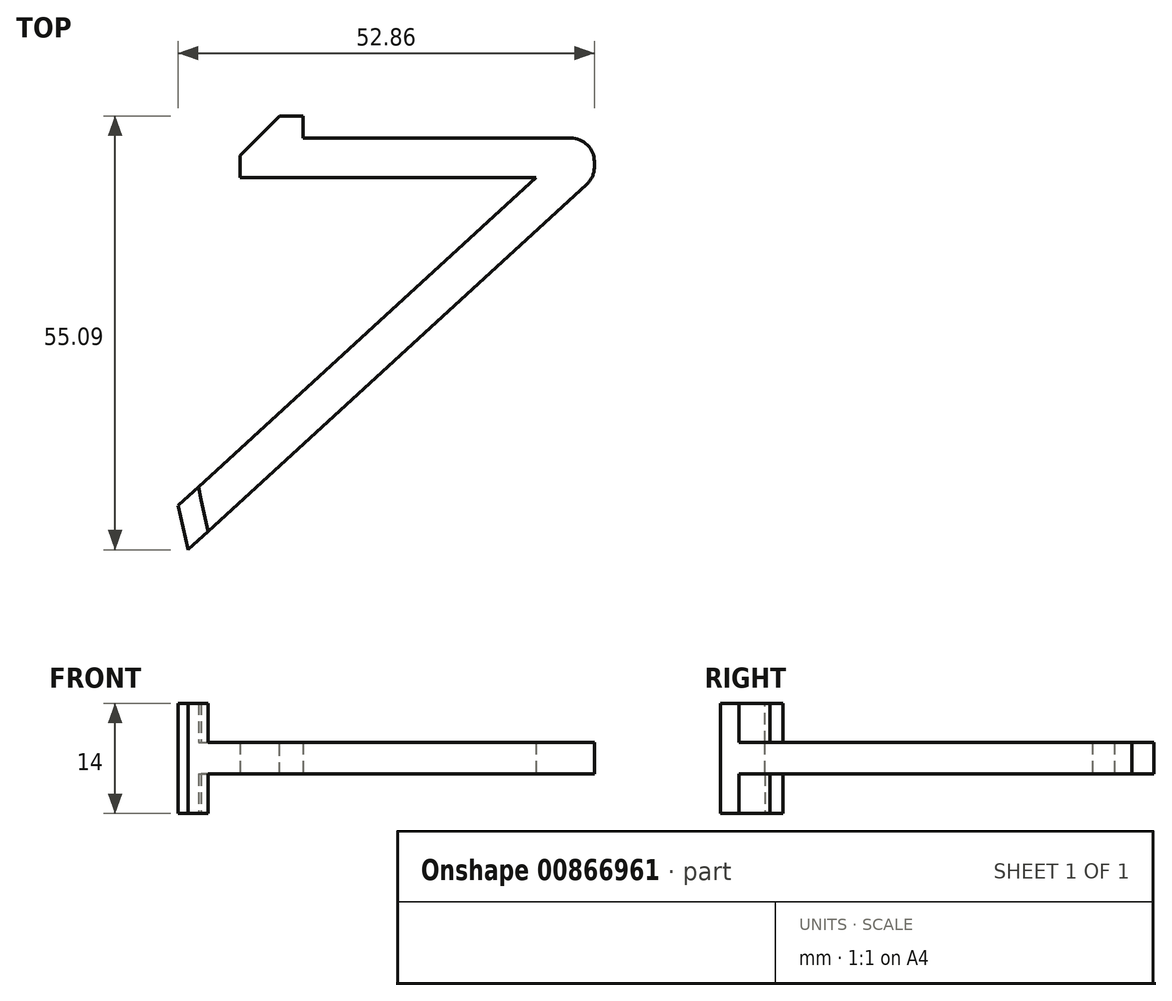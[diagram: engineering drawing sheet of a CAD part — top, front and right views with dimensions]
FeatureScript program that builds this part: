
annotation { "Feature Type Name" : "Feature", "Feature Type Description" : "" }
export const myFeature = defineFeature(function(context is Context, id is Id, definition is map)
    precondition{}
    {
        {
            var Q0;
            Q0=qCreatedBy(makeId("Top.planeOp"),FACE);
            var sketch = newSketch(context, id + "F0", { "sketchPlane" : qUnion([Q0])});
            skLineSegment(sketch, "E0", {"start": v(-40, 0) * mm, "end": v(0, 0) * mm});
            skLineSegment(sketch, "E1", {"start": v(0, 0) * mm, "end": v(0, -5) * mm});
            skLineSegment(sketch, "E2", {"start": v(0, -5) * mm, "end": v(-40, -5) * mm});
            skLineSegment(sketch, "E3", {"start": v(-40, -5) * mm, "end": v(-40, 0) * mm});
            skLineSegment(sketch, "E4", {"start": v(0, -5) * mm, "end": v(-51.6, -52.3) * mm});
            skLineSegment(sketch, "E5", {"start": v(-40, 0) * mm, "end": v(-45, 0) * mm});
            skLineSegment(sketch, "E6", {"start": v(-45, 0) * mm, "end": v(-45, -5) * mm});
            skLineSegment(sketch, "E7", {"start": v(-45, -5) * mm, "end": v(-40, -5) * mm});
            skLineSegment(sketch, "E8", {"start": v(-51.6, -52.3) * mm, "end": v(-54.99, -48.6) * mm});
            skLineSegment(sketch, "E9", {"start": v(-54.99, -48.6) * mm, "end": v(-7.4, -5) * mm});
            skLineSegment(sketch, "E10", {"start": v(-51.6, -52.3) * mm, "end": v(-52.86, -46.65) * mm});
            skSolve(sketch);
        }
        {
            var Q0;
            Q0=makeQuery(id+"F0.imprint","IMPRINT",FACE,{"disambiguationData":[TD([[makeQuery(id+"F0.imprint","IMPRINT",EDGE,{"derivedFrom":sQuery(id+"F0.wireOp",EDGE,"E0")}),-1.0]])]});
            var Q1;
            {var subQ0=sQuery(id+"F0.wireOp",EDGE,"E4");Q1=makeQuery(id+"F0.imprint","IMPRINT",FACE,{"disambiguationData":[TD([[makeQuery(id+"F0.imprint","IMPRINT",EDGE,{"derivedFrom":subQ0}),-1.0]])]});}
            var Q2;
            Q2=makeQuery(id+"F0.imprint","IMPRINT",FACE,{"disambiguationData":[TD([[makeQuery(id+"F0.imprint","IMPRINT",EDGE,{"derivedFrom":sQuery(id+"F0.wireOp",EDGE,"E3")}),1.0]])]});
            extrude(context, id + "F1", {"entities" : qUnion([Q0, Q1, Q2]), "depth" : 4 * mm, "offsetDistance" : 25 * mm});
        }
        {
            var Q0;
            Q0=makeQuery(id+"F1.opExtrude","SWEPT_EDGE",EDGE,{"disambiguationData":[OSD([sQuery(id+"F0.wireOp",EDGE,"E0"),sQuery(id+"F0.wireOp",EDGE,"E1")])]});
            var Q1;
            Q1=makeQuery(id+"F1.opExtrude","SWEPT_EDGE",EDGE,{"disambiguationData":[OSD([sQuery(id+"F0.wireOp",EDGE,"E1"),sQuery(id+"F0.wireOp",EDGE,"E2"),sQuery(id+"F0.wireOp",EDGE,"E4")])]});
            fillet(context, id + "F2", {"entities" : qUnion([Q0, Q1]), "radius" : 3 * mm, "tangentPropagation" : true, "allowEdgeOverflow" : false});
        }
        {
            var Q0;
            Q0=qCreatedBy(makeId("Front.planeOp"),FACE);
            var sketch = newSketch(context, id + "F3", { "sketchPlane" : qUnion([Q0])});
            skLineSegment(sketch, "E11", {"start": v(-45, 0) * mm, "end": v(0, 0) * mm});
            skLineSegment(sketch, "E12", {"start": v(-45, 0) * mm, "end": v(-45, 4) * mm});
            skLineSegment(sketch, "E13", {"start": v(-45, 4) * mm, "end": v(-37, 4) * mm});
            skLineSegment(sketch, "E14", {"start": v(-37, 4) * mm, "end": v(-37, 0) * mm});
            skSolve(sketch);
        }
        {
            var Q0;
            {var subQ0=sQuery(id+"F3.wireOp",EDGE,"E12");Q0=makeQuery(id+"F3.imprint","IMPRINT",FACE,{"disambiguationData":[TD([[makeQuery(id+"F3.imprint","IMPRINT",EDGE,{"derivedFrom":subQ0}),-1.0]])]});}
            extrude(context, id + "F4", {"entities" : qUnion([Q0]), "operationType" : NewBodyOperationType.ADD, "oppositeDirection" : true, "depth" : (6.8 - 4) * mm, "offsetDistance" : 25 * mm});
        }
        {
            var Q0;
            Q0=makeQuery(id+"F4.opExtrude","CAP_EDGE",EDGE,{"disambiguationData":[OSD([sQuery(id+"F3.wireOp",EDGE,"E12")])],"isStart":false});
            chamfer(context, id + "F5", {"entities" : qUnion([Q0]), "width" : 5 * mm, "tangentPropagation" : true});
        }
        {
            var Q0;
            Q0=makeQuery(id+"F1.opExtrude","SWEPT_FACE",FACE,{"disambiguationData":[OSD([sQuery(id+"F0.wireOp",EDGE,"E10")])]});
            cPlane(context, id + "F6", {"entities" : qUnion([Q0]), "cplaneType" : CPlaneType.OFFSET, "offset" : 0 * mm, "width" : 150 * mm, "height" : 150 * mm});
        }
        {
            var Q0;
            Q0=qCreatedBy(id+"F6.planeOp",FACE);
            var sketch = newSketch(context, id + "F7", { "sketchPlane" : qUnion([Q0])});
            skLineSegment(sketch, "E15", {"start": v(34.1, 0) * mm, "end": v(34.1, 4) * mm});
            skLineSegment(sketch, "E16", {"start": v(34.1, 4) * mm, "end": v(39.86, 4) * mm});
            skLineSegment(sketch, "E17", {"start": v(39.86, 4) * mm, "end": v(39.86, 0) * mm});
            skLineSegment(sketch, "E18", {"start": v(39.86, 0) * mm, "end": v(34.1, 0) * mm});
            skLineSegment(sketch, "E19", {"start": v(34.1, 0) * mm, "end": v(34.1, -5) * mm});
            skLineSegment(sketch, "E20", {"start": v(34.1, -5) * mm, "end": v(39.86, -5) * mm});
            skLineSegment(sketch, "E21", {"start": v(39.86, -5) * mm, "end": v(39.86, 0) * mm});
            skLineSegment(sketch, "E22", {"start": v(34.1, 4) * mm, "end": v(34.1, 9) * mm});
            skLineSegment(sketch, "E23", {"start": v(34.1, 9) * mm, "end": v(39.86, 9) * mm});
            skLineSegment(sketch, "E24", {"start": v(39.86, 9) * mm, "end": v(39.86, 4) * mm});
            skSolve(sketch);
        }
        {
            var Q0;
            Q0=makeQuery(id+"F7.imprint","IMPRINT",FACE,{"disambiguationData":[TD([[makeQuery(id+"F7.imprint","IMPRINT",EDGE,{"derivedFrom":sQuery(id+"F7.wireOp",EDGE,"E16")}),1.0]])]});
            var Q1;
            Q1=makeQuery(id+"F7.imprint","IMPRINT",FACE,{"disambiguationData":[TD([[makeQuery(id+"F7.imprint","IMPRINT",EDGE,{"derivedFrom":sQuery(id+"F7.wireOp",EDGE,"E18")}),1.0]])]});
            extrude(context, id + "F8", {"entities" : qUnion([Q0, Q1]), "operationType" : NewBodyOperationType.ADD, "oppositeDirection" : true, "depth" : 3 * mm, "offsetDistance" : 25 * mm});
        }
        {
            var Q0;
            Q0=qCreatedBy(makeId("Top.planeOp"),FACE);
            var sketch = newSketch(context, id + "F9", { "sketchPlane" : qUnion([Q0])});
            skLineSegment(sketch, "E25", {"start": v(0, 0) * mm, "end": v(0, -5) * mm});
            skLineSegment(sketch, "E26", {"start": v(0, -5) * mm, "end": v(-7.4, -5) * mm});
            skLineSegment(sketch, "E27", {"start": v(0, -5) * mm, "end": v(-51.6, -52.3) * mm});
            skLineSegment(sketch, "E28", {"start": v(-48.61, -49.55) * mm, "end": v(-48.08, -51.72) * mm});
            skLineSegment(sketch, "E29", {"start": v(-48.08, -51.72) * mm, "end": v(-51.6, -52.3) * mm});
            skLineSegment(sketch, "E30", {"start": v(-7.4, -5) * mm, "end": v(-59.01, -52.3) * mm});
            skLineSegment(sketch, "E31", {"start": v(-52.85, -46.65) * mm, "end": v(-49.93, -45.99) * mm});
            skLineSegment(sketch, "E32", {"start": v(-49.93, -45.99) * mm, "end": v(-50.3, -44.31) * mm});
            skSolve(sketch);
        }
        {
            var Q0;
            {var subQ2=sQuery(id+"F9.wireOp",EDGE,"E28");Q0=makeQuery(id+"F9.imprint","IMPRINT",FACE,{"disambiguationData":[TD([[makeQuery(id+"F9.imprint","IMPRINT",EDGE,{"derivedFrom":subQ2}),-1.0]])]});}
            extrude(context, id + "F10", {"entities" : qUnion([Q0]), "operationType" : NewBodyOperationType.REMOVE, "depth" : 25 * mm, "offsetDistance" : 25 * mm, "hasSecondDirection" : true, "secondDirectionOppositeDirection" : true, "secondDirectionDepth" : 25 * mm});
        }
        {
            var Q0;
            {var subQ0=sQuery(id+"F9.wireOp",EDGE,"E31");Q0=makeQuery(id+"F9.imprint","IMPRINT",FACE,{"disambiguationData":[TD([[makeQuery(id+"F9.imprint","IMPRINT",EDGE,{"derivedFrom":subQ0}),1.0]])]});}
            extrude(context, id + "F11", {"entities" : qUnion([Q0]), "operationType" : NewBodyOperationType.ADD, "depth" : 9 * mm, "offsetDistance" : 25 * mm, "hasSecondDirection" : true, "secondDirectionOppositeDirection" : true, "secondDirectionDepth" : 5 * mm});
        }
    });
